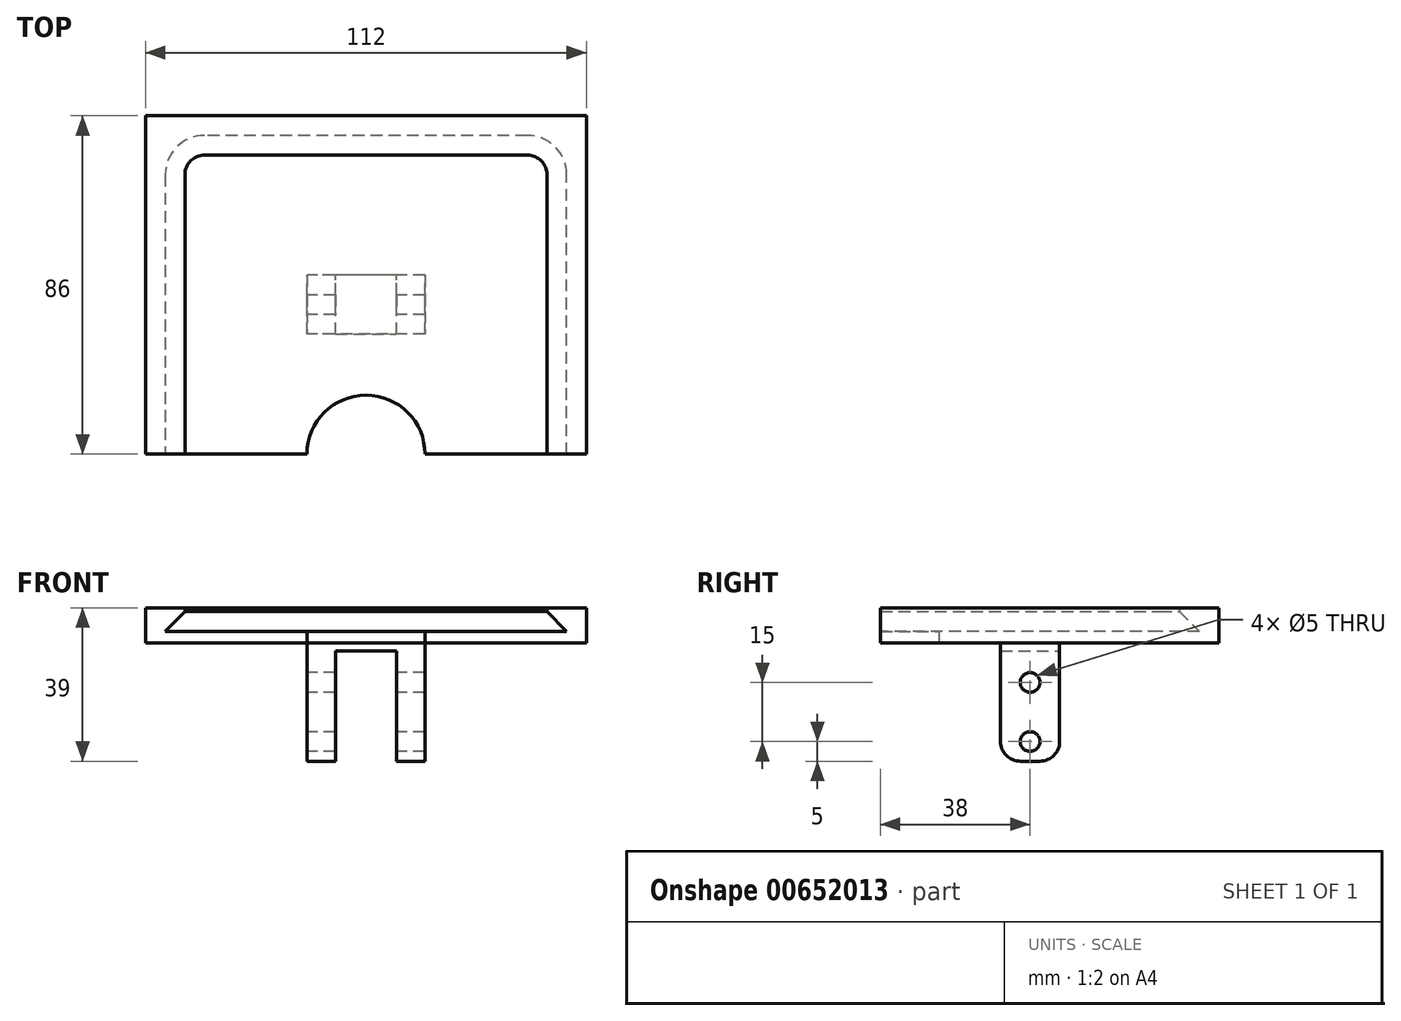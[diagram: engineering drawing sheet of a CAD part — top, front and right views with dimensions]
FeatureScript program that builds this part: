
annotation { "Feature Type Name" : "Feature", "Feature Type Description" : "" }
export const myFeature = defineFeature(function(context is Context, id is Id, definition is map)
    precondition{}
    {
        {
            var Q0;
            Q0=qCreatedBy(makeId("Top.planeOp"),FACE);
            var sketch = newSketch(context, id + "F0", { "sketchPlane" : qUnion([Q0])});
            skLineSegment(sketch, "E0.bottom", {"start": v(-46, 38) * mm, "end": v(46, 38) * mm});
            skLineSegment(sketch, "E0.left", {"start": v(-46, 38) * mm, "end": v(-46, -38) * mm});
            skLineSegment(sketch, "E0.right", {"start": v(46, 38) * mm, "end": v(46, -38) * mm});
            skLineSegment(sketch, "E1.0", {"start": v(56, 48) * mm, "end": v(56, -38) * mm});
            skLineSegment(sketch, "E1.1", {"start": v(-56, 48) * mm, "end": v(56, 48) * mm});
            skLineSegment(sketch, "E1.2", {"start": v(-56, 48) * mm, "end": v(-56, -38) * mm});
            skLineSegment(sketch, "E2", {"start": v(-46, -38) * mm, "end": v(-56, -38) * mm});
            skLineSegment(sketch, "E3", {"start": v(46, -38) * mm, "end": v(56, -38) * mm});
            skSolve(sketch);
        }
        {
            var Q0;
            Q0 = qSketchRegion(id + "F0", true);
            extrude(context, id + "F1", {"entities" : qUnion([Q0]), "depth" : 6 * mm, "offsetDistance" : 25 * mm});
        }
        {
            var Q0;
            Q0=makeQuery(id+"F1.opExtrude","SWEPT_EDGE",EDGE,{"disambiguationData":[OSD([sQuery(id+"F0.wireOp",EDGE,"E0.bottom"),sQuery(id+"F0.wireOp",EDGE,"E0.left")])]});
            var Q1;
            Q1=makeQuery(id+"F1.opExtrude","SWEPT_EDGE",EDGE,{"disambiguationData":[OSD([sQuery(id+"F0.wireOp",EDGE,"E0.bottom"),sQuery(id+"F0.wireOp",EDGE,"E0.right")])]});
            fillet(context, id + "F2", {"entities" : qUnion([Q0, Q1]), "radius" : 5 * mm, "tangentPropagation" : true, "allowEdgeOverflow" : false});
        }
        {
            var Q0;
            Q0=makeQuery(id+"F1.opExtrude","CAP_EDGE",EDGE,{"disambiguationData":[OSD([sQuery(id+"F0.wireOp",EDGE,"E0.left")])],"isStart":true});
            chamfer(context, id + "F3", {"entities" : qUnion([Q0]), "width" : 5 * mm, "tangentPropagation" : true});
        }
        {
            var Q0;
            Q0=qCreatedBy(makeId("Top.planeOp"),FACE);
            var sketch = newSketch(context, id + "F4", { "sketchPlane" : qUnion([Q0])});
            skLineSegment(sketch, "E4.0", {"start": v(-56, 48) * mm, "end": v(-56, -38) * mm});
            skLineSegment(sketch, "E5.0", {"start": v(-56, 48) * mm, "end": v(56, 48) * mm});
            skLineSegment(sketch, "E6.0", {"start": v(56, 48) * mm, "end": v(56, -38) * mm});
            skLineSegment(sketch, "E7", {"start": v(-56, -38) * mm, "end": v(-15, -38) * mm});
            skArc(sketch, "E8", {"start": v(15, -38) * mm, "mid": v(0, -23) * mm, "end": v(-15, -38) * mm});
            skLineSegment(sketch, "E9.trimOffspring", {"start": v(15, -38) * mm, "end": v(56, -38) * mm});
            skSolve(sketch);
        }
        {
            var Q0;
            Q0 = qSketchRegion(id + "F4", true);
            extrude(context, id + "F5", {"entities" : qUnion([Q0]), "operationType" : NewBodyOperationType.ADD, "oppositeDirection" : true, "depth" : 3 * mm, "offsetDistance" : 25 * mm});
        }
        {
            var Q0;
            Q0=qCreatedBy(makeId("Right.planeOp"),FACE);
            var sketch = newSketch(context, id + "F6", { "sketchPlane" : qUnion([Q0])});
            skLineSegment(sketch, "E10.0", {"start": v(48, -3) * mm, "end": v(-38, -3) * mm});
            skCircle(sketch, "E11", {"center": v(0, -13) * mm, "radius": 2.5 * mm});
            skCircle(sketch, "E12", {"center": v(0, -28) * mm, "radius": 2.5 * mm});
            skLineSegment(sketch, "E13.bottom", {"start": v(7.5, -3) * mm, "end": v(-7.5, -3) * mm});
            skLineSegment(sketch, "E13.top", {"start": v(7.5, -33) * mm, "end": v(-7.5, -33) * mm});
            skLineSegment(sketch, "E13.left", {"start": v(7.5, -3) * mm, "end": v(7.5, -33) * mm});
            skLineSegment(sketch, "E13.right", {"start": v(-7.5, -3) * mm, "end": v(-7.5, -33) * mm});
            skSolve(sketch);
        }
        {
            var Q0;
            Q0 = qSketchRegion(id + "F6", true);
            extrude(context, id + "F7", {"entities" : qUnion([Q0]), "endBound" : BoundingType.SYMMETRIC, "depth" : 30 * mm, "offsetDistance" : 25 * mm});
        }
        {
            var Q0;
            Q0 = qSketchRegion(id + "F6", true);
            extrude(context, id + "F8", {"entities" : qUnion([Q0]), "operationType" : NewBodyOperationType.REMOVE, "endBound" : BoundingType.SYMMETRIC, "oppositeDirection" : true, "depth" : 15.5 * mm, "offsetDistance" : 25 * mm});
        }
        {
            var Q0;
            Q0=makeQuery(id+"F5.opExtrude","CAP_FACE",FACE,{"disambiguationData":[OSD([sQuery(id+"F4.wireOp",EDGE,"E4.0"),sQuery(id+"F4.wireOp",EDGE,"E5.0"),sQuery(id+"F4.wireOp",EDGE,"E6.0"),sQuery(id+"F4.wireOp",EDGE,"E7"),sQuery(id+"F4.wireOp",EDGE,"E8"),sQuery(id+"F4.wireOp",EDGE,"E9.trimOffspring")])],"isStart":false});
            var sketch = newSketch(context, id + "F9", { "sketchPlane" : qUnion([Q0])});
            skLineSegment(sketch, "E14.0", {"start": v(-15, -7.5) * mm, "end": v(-15, 7.5) * mm});
            skLineSegment(sketch, "E15.0", {"start": v(15, -7.5) * mm, "end": v(15, 7.5) * mm});
            skLineSegment(sketch, "E16", {"start": v(-15, 7.5) * mm, "end": v(15, 7.5) * mm});
            skLineSegment(sketch, "E17", {"start": v(15, -7.5) * mm, "end": v(-15, -7.5) * mm});
            skSolve(sketch);
        }
        {
            var Q0;
            Q0 = qSketchRegion(id + "F9", true);
            extrude(context, id + "F10", {"entities" : qUnion([Q0]), "operationType" : NewBodyOperationType.ADD, "depth" : 2 * mm, "offsetDistance" : 25 * mm});
        }
        {
            var Q0;
            {var subQ0=sQuery(id+"F6.wireOp",EDGE,"E13.right");var subQ1=sQuery(id+"F6.wireOp",EDGE,"E13.left");var subQ2=sQuery(id+"F6.wireOp",EDGE,"E13.top");var subQ3=sQuery(id+"F6.wireOp",EDGE,"E13.bottom");var subQ4=sQuery(id+"F6.wireOp",EDGE,"E12");var subQ5=sQuery(id+"F6.wireOp",EDGE,"E11");Q0=makeQuery(id+"F8.boolean.opBoolean","SPLIT",EDGE,{"disambiguationData":[TD([makeQuery(id+"F7.opExtrude","CAP_FACE",FACE,{"disambiguationData":[OSD([subQ5,subQ4,subQ3,subQ2,subQ1,subQ0])],"isStart":false})])],"derivedFrom":makeQuery(id+"F7.opExtrude","SWEPT_EDGE",EDGE,{"disambiguationData":[OSD([subQ2,subQ0])]})});}
            var Q1;
            {var subQ0=sQuery(id+"F6.wireOp",EDGE,"E13.right");var subQ1=sQuery(id+"F6.wireOp",EDGE,"E13.left");var subQ2=sQuery(id+"F6.wireOp",EDGE,"E13.top");var subQ3=sQuery(id+"F6.wireOp",EDGE,"E13.bottom");var subQ4=sQuery(id+"F6.wireOp",EDGE,"E12");var subQ5=sQuery(id+"F6.wireOp",EDGE,"E11");Q1=makeQuery(id+"F8.boolean.opBoolean","SPLIT",EDGE,{"disambiguationData":[TD([makeQuery(id+"F7.opExtrude","CAP_FACE",FACE,{"disambiguationData":[OSD([subQ5,subQ4,subQ3,subQ2,subQ1,subQ0])],"isStart":false})])],"derivedFrom":makeQuery(id+"F7.opExtrude","SWEPT_EDGE",EDGE,{"disambiguationData":[OSD([subQ2,subQ1])]})});}
            var Q2;
            {var subQ0=sQuery(id+"F6.wireOp",EDGE,"E13.right");var subQ1=sQuery(id+"F6.wireOp",EDGE,"E13.left");var subQ2=sQuery(id+"F6.wireOp",EDGE,"E13.top");var subQ3=sQuery(id+"F6.wireOp",EDGE,"E13.bottom");var subQ4=sQuery(id+"F6.wireOp",EDGE,"E12");var subQ5=sQuery(id+"F6.wireOp",EDGE,"E11");Q2=makeQuery(id+"F8.boolean.opBoolean","SPLIT",EDGE,{"disambiguationData":[TD([makeQuery(id+"F7.opExtrude","CAP_FACE",FACE,{"disambiguationData":[OSD([subQ5,subQ4,subQ3,subQ2,subQ1,subQ0])],"isStart":true})])],"derivedFrom":makeQuery(id+"F7.opExtrude","SWEPT_EDGE",EDGE,{"disambiguationData":[OSD([subQ2,subQ0])]})});}
            var Q3;
            {var subQ0=sQuery(id+"F6.wireOp",EDGE,"E13.right");var subQ1=sQuery(id+"F6.wireOp",EDGE,"E13.left");var subQ2=sQuery(id+"F6.wireOp",EDGE,"E13.top");var subQ3=sQuery(id+"F6.wireOp",EDGE,"E13.bottom");var subQ4=sQuery(id+"F6.wireOp",EDGE,"E12");var subQ5=sQuery(id+"F6.wireOp",EDGE,"E11");Q3=makeQuery(id+"F8.boolean.opBoolean","SPLIT",EDGE,{"disambiguationData":[TD([makeQuery(id+"F7.opExtrude","CAP_FACE",FACE,{"disambiguationData":[OSD([subQ5,subQ4,subQ3,subQ2,subQ1,subQ0])],"isStart":true})])],"derivedFrom":makeQuery(id+"F7.opExtrude","SWEPT_EDGE",EDGE,{"disambiguationData":[OSD([subQ2,subQ1])]})});}
            fillet(context, id + "F11", {"entities" : qUnion([Q0, Q1, Q2, Q3]), "radius" : 5 * mm, "tangentPropagation" : true, "allowEdgeOverflow" : false});
        }
    });
